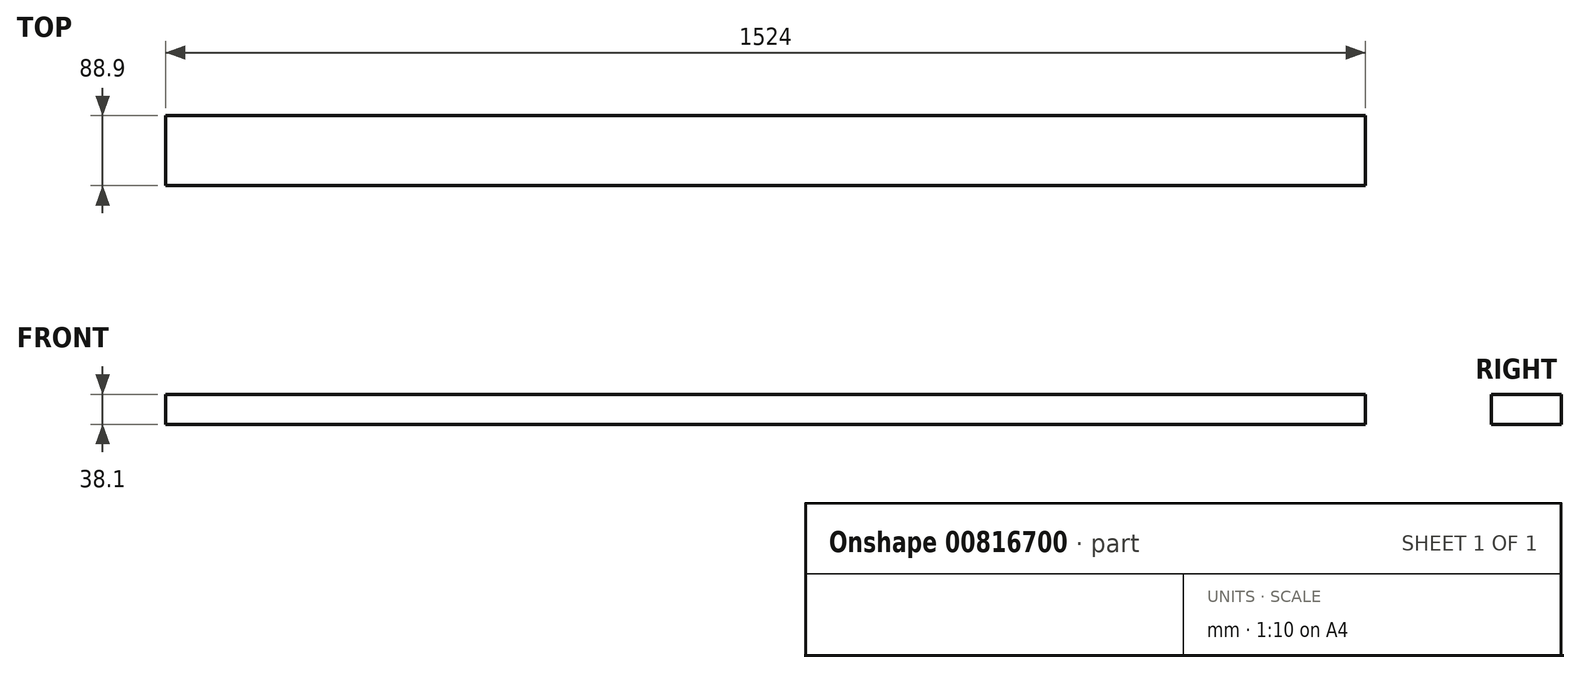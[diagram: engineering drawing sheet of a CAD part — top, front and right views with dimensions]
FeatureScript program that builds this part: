
annotation { "Feature Type Name" : "Feature", "Feature Type Description" : "" }
export const myFeature = defineFeature(function(context is Context, id is Id, definition is map)
    precondition{}
    {
        {
            var Q0;
            Q0=qCreatedBy(makeId("Top.planeOp"),FACE);
            var sketch = newSketch(context, id + "F0", { "sketchPlane" : qUnion([Q0])});
            skLineSegment(sketch, "E0.bottom", {"start": v(0, 0) * mm, "end": v(1524, 0) * mm});
            skLineSegment(sketch, "E0.top", {"start": v(0, 88.9) * mm, "end": v(1524, 88.9) * mm});
            skLineSegment(sketch, "E0.left", {"start": v(0, 0) * mm, "end": v(0, 88.9) * mm});
            skLineSegment(sketch, "E0.right", {"start": v(1524, 0) * mm, "end": v(1524, 88.9) * mm});
            skSolve(sketch);
        }
        {
            var Q0;
            Q0 = qSketchRegion(id + "F0", true);
            extrude(context, id + "F1", {"entities" : qUnion([Q0]), "depth" : 38.1 * mm, "offsetDistance" : 25.4 * mm});
        }
    });
